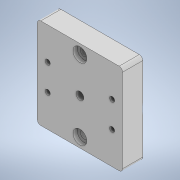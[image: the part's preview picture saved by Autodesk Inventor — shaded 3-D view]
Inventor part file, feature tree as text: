
AUTODESK INVENTOR PART (.ipt)
format: ipt  version: 2020 (Build 240168000, 168)  size: 174,592 bytes
history: native  units: in
note: dims shown in document units (in); Inventor stores cm internally (conversion verified against a paired STEP export)
features: sketch x5, hole x3, extrude x2, fillet x1
ambient origin geometry x8: Origin, YZ Plane, XZ Plane, XY Plane, X Axis, Y Axis, Z Axis, Center Point
bodies: Solid1 (feature_tree)
feature tree (11):
  extrude  "Extrusion1"  Depth=1.0236in
  hole  "Hole1"  [1 undecoded]
  hole  "Hole3"  [1 undecoded]
  fillet  "Fillet1"  Radius=0.8071in
  extrude  "Extrusion3"  Depth=0.8071in
  hole  "Hole5"  [1 undecoded]
  sketch  "Sketch1"  dims[d0=2.0472in d1=1.0236in]
  sketch  "Sketch3"  dims[d2=1.9291in d3=0.9646in]
  sketch  "Sketch5"  dims[d4=0.4547in d5=0.0in d13=0.2165in d14=0.8071in]
  sketch  "Sketch7"  dims[d15=0.2165in d16=0.8071in]
  sketch  "Sketch10"  dims[d17=0.1695in d18=0.224in d19=0.3125in d20=0.0945in d21=0.5635in d22=0.4843in d23=0.0in d31=1.0236in d32=0.9646in d33=0.1772in d34=0.1575in d35=0.315in d36=0.1575in d37=90.0deg d38=0.4646in d39=0.0in d40=0.0787in d57=1.0in d58=0.4862in d59=1.9685in d60=0.0in d77=0.7283in d78=0.2953in d79=0.7283in d80=1.4567in d81=0.7283in d82=0.2953in d83=0.2953in d84=0.2953in d85=0.1142in d86=0.1969in d87=0.2165in d88=0.2953in d89=90.0deg d90=0.4547in d91=0.0in]
note: 3 required parameter values undecoded (feature->parameter linkage not recoverable at this tier; creation-order binding heuristic only, values carry confidence <= 0.55)
